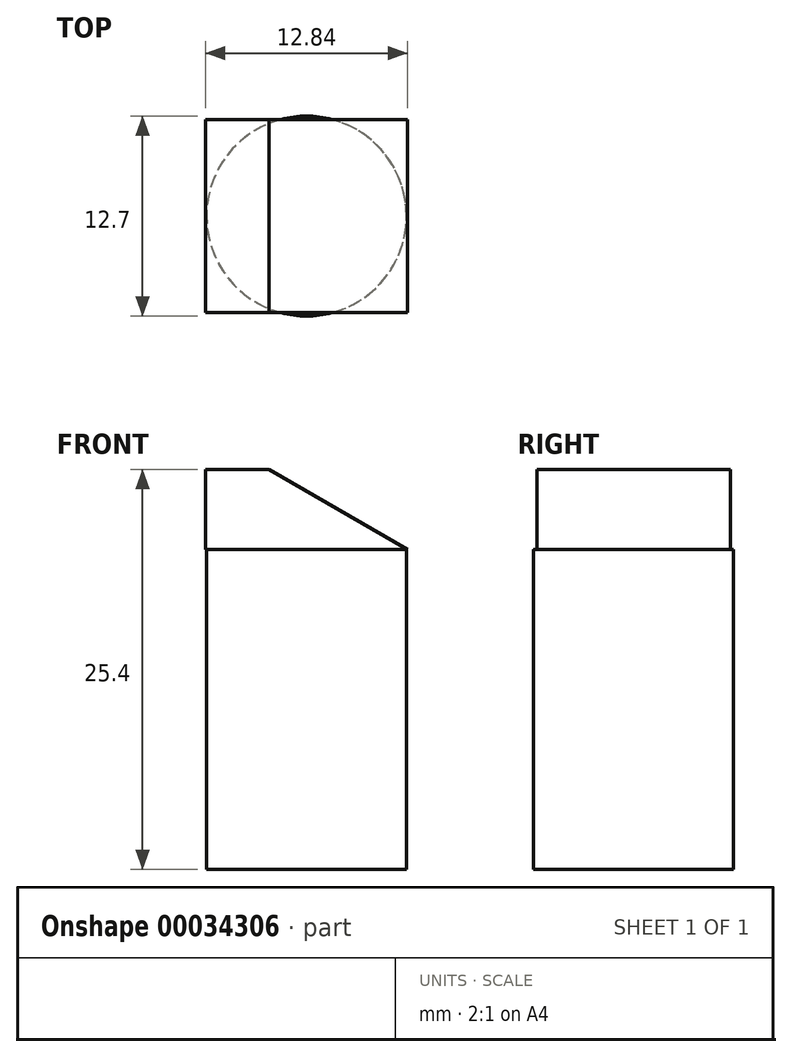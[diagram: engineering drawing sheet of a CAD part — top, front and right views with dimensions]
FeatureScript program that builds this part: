
annotation { "Feature Type Name" : "Feature", "Feature Type Description" : "" }
export const myFeature = defineFeature(function(context is Context, id is Id, definition is map)
    precondition{}
    {
        {
            var Q0;
            Q0=qCreatedBy(makeId("Top.planeOp"),FACE);
            var sketch = newSketch(context, id + "F0", { "sketchPlane" : qUnion([Q0])});
            skCircle(sketch, "E0", {"center": v(0, 0) * mm, "radius": 6.35 * mm});
            skSolve(sketch);
        }
        {
            var Q0;
            Q0 = qSketchRegion(id + "F0", true);
            extrude(context, id + "F1", {"entities" : qUnion([Q0]), "depth" : 20.32 * mm});
        }
        {
            var Q0;
            Q0=makeQuery(id+"F1.opExtrude","CAP_FACE",FACE,{"disambiguationData":[OSD([sQuery(id+"F0.wireOp",EDGE,"E0")])],"isStart":false});
            var sketch = newSketch(context, id + "F2", { "sketchPlane" : qUnion([Q0])});
            skLineSegment(sketch, "E1.rect.bottom", {"start": v(6.42, 6.14) * mm, "end": v(-6.42, 6.14) * mm});
            skLineSegment(sketch, "E1.rect.top", {"start": v(6.42, -6.14) * mm, "end": v(-6.42, -6.14) * mm});
            skLineSegment(sketch, "E1.rect.left", {"start": v(6.42, 6.14) * mm, "end": v(6.42, -6.14) * mm});
            skLineSegment(sketch, "E1.rect.right", {"start": v(-6.42, 6.14) * mm, "end": v(-6.42, -6.14) * mm});
            skPoint(sketch, "E1.rect.middle", {"position": v(0, 0) * mm});
            skSolve(sketch);
        }
        {
            var Q0;
            Q0 = qSketchRegion(id + "F2", true);
            extrude(context, id + "F3", {"entities" : qUnion([Q0]), "operationType" : NewBodyOperationType.ADD, "depth" : 5.08 * mm});
        }
        {
            var Q0;
            Q0=makeQuery(id+"F3.opExtrude","CAP_EDGE",EDGE,{"disambiguationData":[OSD([sQuery(id+"F2.wireOp",EDGE,"E1.rect.left")])],"isStart":false});
            chamfer(context, id + "F4", {"entities" : qUnion([Q0]), "chamferType" : ChamferType.OFFSET_ANGLE, "width" : 5.08 * mm, "oppositeDirection" : false, "angle" : 60 * degree, "tangentPropagation" : true});
        }
    });
